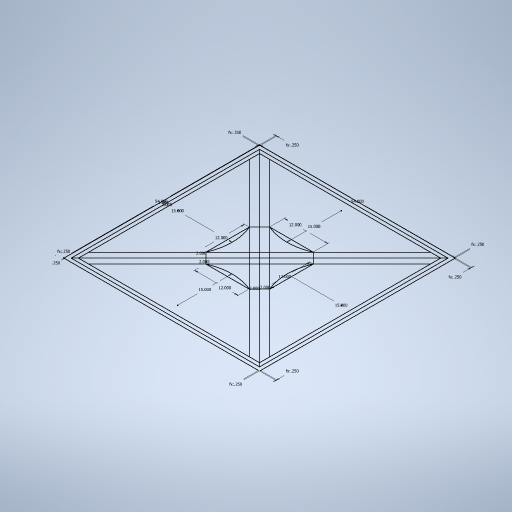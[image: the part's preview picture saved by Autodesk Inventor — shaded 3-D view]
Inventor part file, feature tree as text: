
AUTODESK INVENTOR PART (.ipt)
format: ipt  version: 2023 (Build 270158000, 158)  size: 275,456 bytes
history: native  units: in
note: dims shown in document units (in); Inventor stores cm internally (conversion verified against a paired STEP export)
features: sketch x2
ambient origin geometry x8: Origin, YZ Plane, XZ Plane, XY Plane, X Axis, Y Axis, Z Axis, Center Point
feature tree (2):
  sketch  "Sketch1"  dims[d0=54.0in]
  sketch  "Sketch2"  dims[d1=54.0in d2=1.0in d3=1.0in d34=0.25in d35=0.25in d36=0.25in d37=0.25in d38=0.25in d39=0.25in d40=0.25in d41=0.25in d42=2.0in d43=2.0in d44=2.0in d45=2.0in d46=12.0in d47=12.0in d48=12.0in d50=12.0in d51=15.0in d52=15.0in d53=15.0in d54=15.0in]
